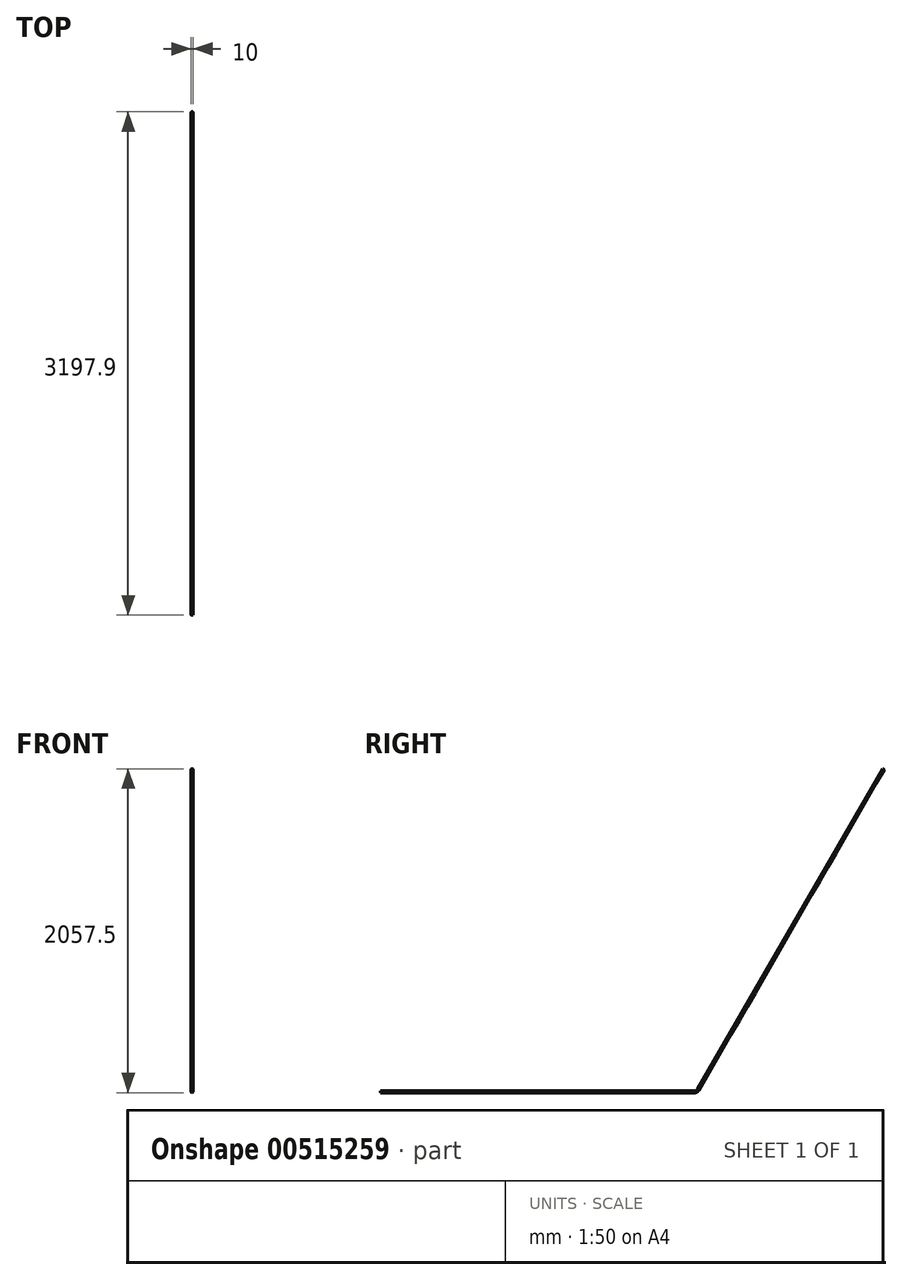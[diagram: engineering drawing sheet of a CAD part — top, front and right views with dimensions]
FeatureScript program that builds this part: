
annotation { "Feature Type Name" : "Feature", "Feature Type Description" : "" }
export const myFeature = defineFeature(function(context is Context, id is Id, definition is map)
    precondition{}
    {
        {
            var Q0;
            Q0=qCreatedBy(makeId("Right.planeOp"),FACE);
            var sketch = newSketch(context, id + "F0", { "sketchPlane" : qUnion([Q0])});
            skLineSegment(sketch, "E0", {"start": v(0, 2050) * mm, "end": v(0, 25) * mm});
            skLineSegment(sketch, "E1", {"start": v(25, 0) * mm, "end": v(1995.57, 0) * mm});
            skPoint(sketch, "E2.visualSharp", {"position": v(0, 0) * mm});
            skArc(sketch, "E2.filletArc", {"start": v(0, 25) * mm, "mid": v(7.32, 7.32) * mm, "end": v(25, 0) * mm});
            skLineSegment(sketch, "E3", {"start": v(2017.22, 12.5) * mm, "end": v(3193.57, 2050) * mm});
            skPoint(sketch, "E4.visualSharp", {"position": v(2010, 0) * mm});
            skArc(sketch, "E4.filletArc", {"start": v(1995.57, 0) * mm, "mid": v(2008.07, 3.35) * mm, "end": v(2017.22, 12.5) * mm});
            skLineSegment(sketch, "E5", {"start": v(0, 2050) * mm, "end": v(3193.57, 2050) * mm, "construction": true});
            skLineSegment(sketch, "E6", {"start": v(25, 0) * mm, "end": v(0, 0) * mm});
            skSolve(sketch);
        }
        {
            var Q0;
            Q0=qCreatedBy(makeId("Top.planeOp"),FACE);
            var Q1;
            Q1=sQuery(id+"F0.wireOp",VERTEX,"E0.start");
            cPlane(context, id + "F1", {"entities" : qUnion([Q0, Q1]), "cplaneType" : CPlaneType.PLANE_POINT, "offset" : 25 * mm, "width" : 150 * mm, "height" : 150 * mm});
        }
        {
            var Q0;
            Q0=qCreatedBy(makeId("Front.planeOp"),FACE);
            var sketch = newSketch(context, id + "F2", { "sketchPlane" : qUnion([Q0])});
            skCircle(sketch, "E7", {"center": v(0, 0) * mm, "radius": 5 * mm});
            skSolve(sketch);
        }
        {
            var Q0;
            Q0=makeQuery(id+"F2.imprint","IMPRINT",FACE,{"disambiguationData":[TD([[makeQuery(id+"F2.imprint","IMPRINT",EDGE,{"derivedFrom":sQuery(id+"F2.wireOp",EDGE,"E7")}),1.0]])]});
            var Q1;
            Q1=sQuery(id+"F0.wireOp",EDGE,"E6");
            var Q2;
            Q2=sQuery(id+"F0.wireOp",EDGE,"E1");
            var Q3;
            Q3=sQuery(id+"F0.wireOp",EDGE,"E4.filletArc");
            var Q4;
            Q4=sQuery(id+"F0.wireOp",EDGE,"E3");
            sweep(context, id + "F3", {"profiles" : qUnion([Q0]), "path" : qUnion([Q1, Q2, Q3, Q4])});
        }
    });
